# Revit family: Haworth_JanusCafe_StandardHeight_Rectangular_Demi-Sec Grande Base
name_source: partatom
category: Furniture
revit_build: Autodesk Revit 2018 (Build: 20170223_1515(x64)
units: mm (PartAtom-declared; Revit-internal decimal feet)

## family parameters
Always vertical = Yes
Cut with Voids When Loaded = No
OmniClass Number = 23.40.70.14.64.21
OmniClass Title = Systems Furniture
Room Calculation Point = No
Shared = No
Work Plane-Based = No

## types (4) — shared parameters
Actual Height = 29 1/2"
Assembly Code = E2020200
Base Finish = Haworth _ Metal _ JanusCafe _ Brushed Stainless Steel JS1-STLS
Manufacturer = Haworth
Revision Number = 2
Ring Finish = Haworth _ Polymer _ Black
Size = Verify Final Dim. w/ Haworth
Table Thickness = 29 1/8"
Top Finish = Haworth _ Laminate _ JanusCafe _ White JH2-1
URL = http://www.haworth.com
URL - Product = https://www.haworth.com
Warranty = https://www.haworth.com

## per-type parameters (varying)
| type | Actual Depth | Actual Width | Description | Large Square | Model | Rectangle | Reducer Ring | Small Square | With Top |
| HCJC-JC-DGP1-Q3030NH - 29h 30w | 30" | 30" | Haworth JanusCafe Square Table 30" - Standard Height - Demi-Sec Grande Base | No | HCJC-JC-DGP1-Q3030NH | No | No | Yes | Yes |
| HCJC-JC-DGP1-Q3636NH - 29h 36w | 36" | 36" | Haworth JanusCafe Square Table 36" - Standard Height - Demi-Sec Grande Base | Yes | HCJC-JC-DGP1-Q3636NH | No | No | No | Yes |
| HCJC-JC-DUP1-Q3636UC - 29h 36w | 36" | 36" | Haworth JanusCafe Square Table 30" w Umbrella- Standard Height - Demi-Sec Grande Base | Yes | HCJC-JC-DUP1-Q3636UC | No | Yes | No | No |
| HCJC-JC-DGP1-R3036NH - 29h 36w | 30" | 36" | Haworth JanusCafe Rectangle Table 30" - Standard Height - Demi-Sec Grande Base | No | HCJC-JC-DGP1-R3036NH | Yes | No | No | Yes |

## geometry (parser evidence)
native form markers: Sweep x3
no freeform markers — native parametric forms only
